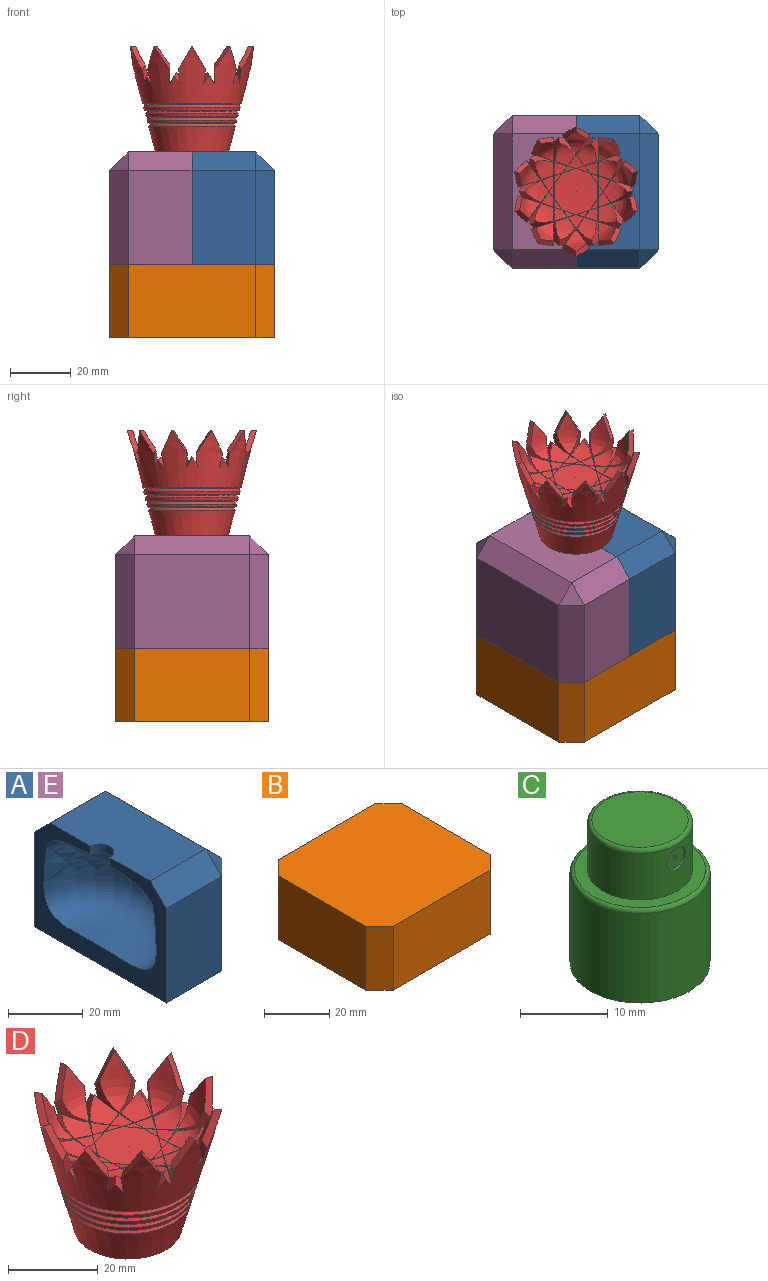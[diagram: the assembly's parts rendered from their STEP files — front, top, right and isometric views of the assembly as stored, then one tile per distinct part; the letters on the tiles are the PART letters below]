
ASSEMBLY  parts=5 mates=5
PART A: 15 faces, bbox 27x50x37 mm
  f0: plane 38x21mm, normal (0,0,1), area 776.5mm2, adj f4,f5,f10,f12,f13
  f1: plane 31x21mm, normal (0,1,0), area 651mm2, adj f3,f5,f9,f12
  f2: plane 31x21mm, normal (0,-1,0), area 651mm2, adj f3,f4,f7,f12
  f3: plane 50x27mm, normal (0,0,-1), area 1314mm2, adj f1,f2,f6,f7,f9,f12
  f4: plane 21x6mm, normal (0,-0.71,0.71), area 178.2mm2, adj f0,f2,f8,f12
  f5: plane 21x6mm, normal (0,0.71,0.71), area 178.2mm2, adj f0,f1,f11,f12
  f6: plane 38x31mm, normal (1,0,0), area 1178mm2, adj f3,f7,f9,f10
  f7: plane 31x6mm, normal (0.71,-0.71,0), area 263mm2, adj f2,f3,f6,f8
  f8: plane 6x6mm, normal (0.58,-0.58,0.58), area 31.2mm2, adj f4,f7,f10
  f9: plane 31x6mm, normal (0.71,0.71,0), area 263mm2, adj f1,f3,f6,f11
  f10: plane 38x6mm, normal (0.71,0,0.71), area 322.4mm2, adj f0,f6,f8,f11
  f11: plane 6x6mm, normal (0.58,0.58,0.58), area 31.2mm2, adj f5,f9,f10
  f12: plane 50x37mm, normal (-1,0,0), area 677.3mm2, adj f0,f1,f2,f3,f4,f5,f13,f14
  f13: cylinder r=3.7mm len=7.4mm, axis (0,0,1), area 30.8mm2, adj f0,f12,f14
  f14: revolved ~42.55x28.46mm, area 2704.3mm2, adj f12,f13
PART B: 10 faces, bbox 54x50x24 mm
  f0: plane 38x24mm, normal (1,0,0), area 912mm2, adj f4,f5,f7,f8
  f1: plane 42x24mm, normal (0,1,0), area 1008mm2, adj f4,f5,f8,f9
  f2: plane 38x24mm, normal (-1,0,0), area 912mm2, adj f4,f5,f6,f9
  f3: plane 42x24mm, normal (0,-1,0), area 1008mm2, adj f4,f5,f6,f7
  f4: plane 54x50mm, normal (0,0,1), area 2628mm2, adj f0,f1,f2,f3,f6,f7,f8,f9
  f5: plane 54x50mm, normal (0,0,-1), area 2628mm2, adj f0,f1,f2,f3,f6,f7,f8,f9
  f6: plane 24x6mm, normal (-0.71,-0.71,0), area 203.6mm2, adj f2,f3,f4,f5
  f7: plane 24x6mm, normal (0.71,-0.71,0), area 203.6mm2, adj f0,f3,f4,f5
  f8: plane 24x6mm, normal (0.71,0.71,0), area 203.6mm2, adj f0,f1,f4,f5
  f9: plane 24x6mm, normal (-0.71,0.71,0), area 203.6mm2, adj f1,f2,f4,f5
PART C: 11 faces, bbox 17.3x17.3x20 mm
  f0: cylinder r=6mm len=12mm, axis (0,0,-1), area 237.9mm2, adj f3,f5,f10
  f1: plane 11x11mm, normal (0,0,1), area 95mm2, adj f10
  f2: cylinder r=8mm len=16mm, axis (0,0,-1), area 628.3mm2, adj f4,f9
  f3: plane 15x15mm, normal (0,0,1), area 63.6mm2, adj f0,f9
  f4: plane 16x16mm, normal (0,0,-1), area 201.1mm2, adj f2
  f5: cylinder r=1.5mm len=3mm, axis (0,-1,0), area 2.9mm2, adj f0,f6
  f6: plane 3x3mm, normal (0,-1,0), area 6.9mm2, adj f5,f8
  f7: plane 0.5x0.5mm, normal (0,-1,0), area 0.2mm2, adj f8
  f8: cylinder r=0.25mm len=4.3mm, axis (0,-1,0), area 6.8mm2, adj f6,f7
  f9: torus R=7.5mm, axis (0,0,1), area 38.6mm2, adj f2,f3
  f10: torus R=5.5mm, axis (0,0,1), area 28.7mm2, adj f0,f1
PART D: 217 faces, bbox 44x44x36.3 mm
  f0: cone r=21.27mm half-angle=14.8deg, axis (0,0,1), area 1549.5mm2, adj f1,f16,f17,f18,f19,f20,f21,f22
  f1: cone r=15.29mm half-angle=67.7deg, axis (0,0,1), area 99mm2, adj f0,f2
  f2: cone r=15.91mm half-angle=38deg, axis (0,0,-1), area 98mm2, adj f1,f3
  f3: cone r=15.65mm half-angle=14.8deg, axis (0,0,1), area 99.1mm2, adj f2,f4
  f4: cone r=14.73mm half-angle=67.7deg, axis (0,0,1), area 95.4mm2, adj f3,f5
  f5: cone r=15.34mm half-angle=38deg, axis (0,0,-1), area 94.5mm2, adj f4,f6
  f6: cone r=15.09mm half-angle=14.8deg, axis (0,0,1), area 95.6mm2, adj f5,f7
  f7: cone r=14.16mm half-angle=67.7deg, axis (0,0,1), area 91.9mm2, adj f6,f8
  f8: cone r=14.78mm half-angle=38deg, axis (0,0,-1), area 90.9mm2, adj f7,f9
  f9: cone r=14.54mm half-angle=14.8deg, axis (0,0,1), area 85mm2, adj f8,f10
  f10: cone r=13.62mm half-angle=67.7deg, axis (0,0,1), area 88.5mm2, adj f9,f11
  f11: cone r=14.23mm half-angle=38deg, axis (0,0,-1), area 87.5mm2, adj f10,f12
  f12: cone r=14.23mm half-angle=14.8deg, axis (0,0,1), area 718.1mm2, adj f11,f13
  f13: plane 24x24mm, normal (0,0,-1), area 225.4mm2, adj f12,f14
  f14: cylinder r=8.5mm len=21mm, axis (0,0,-1), area 1121.5mm2, adj f13,f15
  f15: plane 17x17mm, normal (0,0,-1), area 227mm2, adj f14
  f16: plane 8.04x4.86mm, normal (-0.86,0,0.51), area 14.8mm2, adj f0,f17,f73,f188
  f17: plane 8.04x4.86mm, normal (0.86,0,0.51), area 14.8mm2, adj f0,f16,f70,f188
  f18: plane 8.04x5.58mm, normal (-0.7,0.51,0.51), area 14.8mm2, adj f0,f65,f67,f182
  f19: plane 7.89x7.71mm, normal (0.81,-0.59,0), area 18.8mm2, adj f0,f20,f59,f60,f198
  f20: plane 7.77x4.78mm, normal (-0.7,0.51,0.51), area 15.5mm2, adj f0,f19,f66,f133,f178
  f21: plane 6.38x6.32mm, normal (0.7,0.51,0.51), area 15.5mm2, adj f0,f23,f26,f92,f211
  f22: plane 8.04x4.86mm, normal (0.86,0,0.51), area 14.8mm2, adj f0,f27,f38,f206
  f23: plane 7.89x7.71mm, normal (-0.81,-0.59,0), area 18.8mm2, adj f0,f21,f27,f38,f206
  f24: plane 8.04x5.58mm, normal (-0.7,-0.51,0.51), area 14.8mm2, adj f0,f28,f30,f209
  f25: plane 9.38x7.71mm, normal (1,0,0), area 18.8mm2, adj f0,f26,f28,f30,f209
  f26: plane 8.5x4.17mm, normal (-0.86,0,0.51), area 15.5mm2, adj f0,f21,f25,f110,f211
  f27: plane 8.04x4.86mm, normal (-0.86,0,0.51), area 14.8mm2, adj f0,f22,f23,f206
  f28: plane 8.04x5.52mm, normal (0.7,0.51,0.51), area 14.8mm2, adj f0,f24,f25,f209
  f29: plane 8.47x4.17mm, normal (0.27,0.82,0.51), area 15.5mm2, adj f0,f30,f31,f113,f208
  f30: plane 9x7.71mm, normal (-0.31,-0.95,0), area 18.8mm2, adj f0,f24,f25,f29,f209
  f31: plane 7.77x4.78mm, normal (-0.7,-0.51,0.51), area 15.5mm2, adj f0,f29,f32,f114,f208
  f32: plane 7.89x7.71mm, normal (0.81,0.59,0), area 18.8mm2, adj f0,f31,f34,f35,f207
  f33: plane 7.76x4.44mm, normal (-0.27,0.82,0.51), area 15.5mm2, adj f0,f34,f61,f124,f197
  f34: plane 9x7.71mm, normal (0.31,-0.95,0), area 18.8mm2, adj f0,f32,f33,f36,f207
  f35: plane 8.04x5.12mm, normal (0.27,0.82,0.51), area 14.8mm2, adj f0,f32,f36,f207
  f36: plane 8.04x5.44mm, normal (-0.27,-0.82,0.51), area 14.8mm2, adj f0,f34,f35,f207
  f37: plane 8.04x5.44mm, normal (-0.27,0.82,0.51), area 14.8mm2, adj f0,f59,f60,f198
  f38: plane 7.89x7.71mm, normal (0.81,-0.59,0), area 18.8mm2, adj f0,f22,f23,f39,f206
  f39: plane 6.38x6.32mm, normal (-0.7,0.51,0.51), area 15.5mm2, adj f0,f38,f41,f97,f205
  f40: plane 9.38x7.71mm, normal (-1,0,0), area 18.8mm2, adj f0,f41,f56,f57,f201
  f41: plane 8.5x4.17mm, normal (0.86,0,0.51), area 15.5mm2, adj f0,f39,f40,f99,f205
  f42: plane 8.04x5.58mm, normal (0.7,-0.51,0.51), area 14.8mm2, adj f0,f56,f57,f201
  f43: plane 8.04x5.12mm, normal (-0.27,0.82,0.51), area 14.8mm2, adj f0,f45,f46,f204
  f44: plane 7.77x4.78mm, normal (0.7,-0.51,0.51), area 15.5mm2, adj f0,f46,f58,f120,f200
  f45: plane 8.04x5.44mm, normal (0.27,-0.82,0.51), area 14.8mm2, adj f0,f43,f47,f204
  f46: plane 7.89x7.71mm, normal (-0.81,0.59,0), area 18.8mm2, adj f0,f43,f44,f47,f204
  f47: plane 9x7.71mm, normal (-0.31,-0.95,0), area 18.8mm2, adj f0,f45,f46,f48,f204
  f48: plane 7.76x4.44mm, normal (0.27,0.82,0.51), area 15.5mm2, adj f0,f47,f50,f117,f203
  f49: plane 9x7.71mm, normal (-0.31,0.95,0), area 18.8mm2, adj f0,f50,f54,f55,f202
  f50: plane 7.76x4.44mm, normal (0.27,-0.82,0.51), area 15.5mm2, adj f0,f48,f49,f118,f203
  f51: plane 8.04x5.12mm, normal (-0.27,-0.82,0.51), area 14.8mm2, adj f0,f54,f55,f202
  f52: plane 8.04x5.58mm, normal (0.7,0.51,0.51), area 14.8mm2, adj f0,f62,f63,f191
  f53: plane 7.77x4.78mm, normal (0.7,0.51,0.51), area 15.5mm2, adj f0,f54,f64,f131,f192
  f54: plane 7.89x7.71mm, normal (-0.81,-0.59,0), area 18.8mm2, adj f0,f49,f51,f53,f202
  f55: plane 8.04x5.44mm, normal (0.27,0.82,0.51), area 14.8mm2, adj f0,f49,f51,f202
  f56: plane 9x7.71mm, normal (0.31,-0.95,0), area 18.8mm2, adj f0,f40,f42,f58,f201
  f57: plane 8.04x5.52mm, normal (-0.7,0.51,0.51), area 14.8mm2, adj f0,f40,f42,f201
  f58: plane 8.47x4.17mm, normal (-0.27,0.82,0.51), area 15.5mm2, adj f0,f44,f56,f106,f200
  f59: plane 9x7.71mm, normal (0.31,0.95,0), area 18.8mm2, adj f0,f19,f37,f61,f198
  f60: plane 8.04x5.12mm, normal (0.27,-0.82,0.51), area 14.8mm2, adj f0,f19,f37,f198
  f61: plane 7.76x4.44mm, normal (-0.27,-0.82,0.51), area 15.5mm2, adj f0,f33,f59,f78,f197
  f62: plane 9x7.71mm, normal (0.31,0.95,0), area 18.8mm2, adj f0,f52,f64,f68,f191
  f63: plane 8.04x5.52mm, normal (-0.7,-0.51,0.51), area 14.8mm2, adj f0,f52,f68,f191
  f64: plane 8.47x4.17mm, normal (-0.27,-0.82,0.51), area 15.5mm2, adj f0,f53,f62,f140,f192
  f65: plane 8.04x5.52mm, normal (0.7,-0.51,0.51), area 14.8mm2, adj f0,f18,f75,f182
  f66: plane 8.47x4.17mm, normal (0.27,-0.82,0.51), area 15.5mm2, adj f0,f20,f67,f173,f178
  f67: plane 9x7.71mm, normal (-0.31,0.95,0), area 18.8mm2, adj f0,f18,f66,f75,f182
  f68: plane 9.38x7.71mm, normal (-1,0,0), area 18.8mm2, adj f0,f62,f63,f69,f191
  f69: plane 8.5x4.17mm, normal (0.86,0,0.51), area 15.5mm2, adj f0,f68,f71,f143,f185
  f70: plane 7.89x7.71mm, normal (0.81,0.59,0), area 18.8mm2, adj f0,f17,f71,f73,f188
  f71: plane 6.38x6.32mm, normal (-0.7,-0.51,0.51), area 15.5mm2, adj f0,f69,f70,f168,f185
  f72: plane 6.38x6.32mm, normal (0.7,-0.51,0.51), area 15.5mm2, adj f0,f73,f74,f165,f183
  f73: plane 7.89x7.71mm, normal (-0.81,0.59,0), area 18.8mm2, adj f0,f16,f70,f72,f188
  f74: plane 8.5x4.17mm, normal (-0.86,0,0.51), area 15.5mm2, adj f0,f72,f75,f161,f183
  f75: plane 9.38x7.71mm, normal (1,0,0), area 18.8mm2, adj f0,f65,f67,f74,f182
  f76: plane 2.64x1.99mm, normal (0.81,-0.59,0), area 0.2mm2, adj f77,f125,f127,f195
  f77: plane 2.62x1.98mm, normal (-0.7,0.51,0.51), area 0.3mm2, adj f76,f134,f175,f176
  f78: plane 4.38x3.34mm, normal (0.81,-0.59,0), area 1.4mm2, adj f61,f79,f124,f197
  f79: plane 4.31x3.32mm, normal (-0.7,0.51,0.51), area 1.5mm2, adj f78,f132,f135,f180
  f80: plane 3.03x1.18mm, normal (-0.27,0.82,0.51), area 0.3mm2, adj f81,f87,f88,f216
  f81: plane 3.05x1.18mm, normal (0.31,-0.95,0), area 0.2mm2, adj f80,f82,f96,f214
  f82: plane 3.05x1.18mm, normal (-0.31,-0.95,0), area 0.2mm2, adj f81,f83,f93,f214
  f83: plane 3.03x1.18mm, normal (0.27,0.82,0.51), area 0.3mm2, adj f82,f85,f95,f215
  f84: plane 5.19x2.19mm, normal (-0.27,0.82,0.51), area 0.1mm2, adj f85,f86,f91,f177
  f85: plane 5.19x2.17mm, normal (0.31,-0.95,0), area 0.1mm2, adj f83,f84,f95,f215
  f86: plane 5.19x2.19mm, normal (0.27,0.82,0.51), area 0.1mm2, adj f84,f87,f100,f177
  f87: plane 5.19x2.17mm, normal (-0.31,-0.95,0), area 0.1mm2, adj f80,f86,f88,f216
  f88: plane 2.62x2.01mm, normal (0.7,0.51,0.51), area 0.3mm2, adj f80,f87,f89,f216
  f89: plane 2.64x1.99mm, normal (-0.81,-0.59,0), area 0.2mm2, adj f88,f98,f105,f212
  f90: plane 4.52x3.48mm, normal (0.81,-0.59,0), area 0.1mm2, adj f91,f109,f126,f196
  f91: plane 4.53x3.5mm, normal (-0.7,0.51,0.51), area 0.1mm2, adj f84,f90,f174,f177
  f92: plane 4.38x3.34mm, normal (0.81,-0.59,0), area 1.4mm2, adj f21,f93,f110,f211
  f93: plane 4.33x3.27mm, normal (-0.7,0.51,0.51), area 1.5mm2, adj f82,f92,f96,f214
  f94: plane 2.64x1.99mm, normal (0.81,-0.59,0), area 0.2mm2, adj f95,f108,f111,f210
  f95: plane 2.62x2.01mm, normal (-0.7,0.51,0.51), area 0.3mm2, adj f83,f85,f94,f215
  f96: plane 4.33x3.27mm, normal (0.7,0.51,0.51), area 1.5mm2, adj f81,f93,f97,f214
  f97: plane 4.38x3.34mm, normal (-0.81,-0.59,0), area 1.4mm2, adj f39,f96,f99,f205
  f98: plane 4.97x2.02mm, normal (-0.27,0.82,0.51), area 1.5mm2, adj f89,f99,f107,f212
  f99: plane 5.05x2.03mm, normal (0.31,-0.95,0), area 1.4mm2, adj f41,f97,f98,f205
  f100: plane 4.53x3.5mm, normal (0.7,0.51,0.51), area 0.1mm2, adj f86,f101,f137,f177
  f101: plane 4.52x3.48mm, normal (-0.81,-0.59,0), area 0.1mm2, adj f100,f103,f104,f213
  f102: plane 3.19x0.42mm, normal (-1,0,0), area 0.2mm2, adj f103,f121,f122,f199
  f103: plane 3.18x0.4mm, normal (0.86,0,0.51), area 0.3mm2, adj f101,f102,f104,f213
  f104: plane 3.03x1.23mm, normal (0.27,0.82,0.51), area 0.3mm2, adj f101,f103,f105,f213
  f105: plane 3.05x1.18mm, normal (-0.31,-0.95,0), area 0.2mm2, adj f89,f104,f107,f212
  f106: plane 5.28x1.14mm, normal (-1,0,0), area 1.4mm2, adj f58,f107,f120,f200
  f107: plane 5.2x1.02mm, normal (0.86,0,0.51), area 1.5mm2, adj f98,f105,f106,f212
  f108: plane 3.05x1.18mm, normal (0.31,-0.95,0), area 0.2mm2, adj f94,f109,f112,f210
  f109: plane 3.03x1.23mm, normal (-0.27,0.82,0.51), area 0.3mm2, adj f90,f108,f126,f196
  f110: plane 5.05x2.03mm, normal (-0.31,-0.95,0), area 1.4mm2, adj f26,f92,f111,f211
  f111: plane 4.97x2.02mm, normal (0.27,0.82,0.51), area 1.5mm2, adj f94,f110,f112,f210
  f112: plane 5.2x1.02mm, normal (-0.86,0,0.51), area 1.5mm2, adj f108,f111,f113,f210
  f113: plane 5.28x1.14mm, normal (1,0,0), area 1.4mm2, adj f29,f112,f114,f208
  f114: plane 5.05x2.03mm, normal (0.31,-0.95,0), area 1.4mm2, adj f31,f113,f115,f208
  f115: plane 4.98x2.12mm, normal (-0.27,0.82,0.51), area 1.5mm2, adj f114,f125,f127,f195
  f116: plane 4.31x3.32mm, normal (0.7,-0.51,0.51), area 1.5mm2, adj f117,f121,f122,f199
  f117: plane 4.38x3.34mm, normal (-0.81,0.59,0), area 1.4mm2, adj f48,f116,f118,f203
  f118: plane 4.38x3.34mm, normal (-0.81,-0.59,0), area 1.4mm2, adj f50,f117,f119,f203
  f119: plane 4.31x3.32mm, normal (0.7,0.51,0.51), area 1.5mm2, adj f118,f129,f130,f193
  f120: plane 5.05x2.03mm, normal (-0.31,-0.95,0), area 1.4mm2, adj f44,f106,f121,f200
  f121: plane 4.98x2.12mm, normal (0.27,0.82,0.51), area 1.5mm2, adj f102,f116,f120,f199
  f122: plane 2.64x1.99mm, normal (-0.81,-0.59,0), area 0.2mm2, adj f102,f116,f123,f199
  f123: plane 2.62x1.98mm, normal (0.7,0.51,0.51), area 0.3mm2, adj f122,f128,f136,f194
  f124: plane 4.38x3.34mm, normal (0.81,0.59,0), area 1.4mm2, adj f33,f78,f125,f197
  f125: plane 4.31x3.32mm, normal (-0.7,-0.51,0.51), area 1.5mm2, adj f76,f115,f124,f195
  f126: plane 3.18x0.4mm, normal (-0.86,0,0.51), area 0.3mm2, adj f90,f109,f127,f196
  f127: plane 3.19x0.42mm, normal (1,0,0), area 0.2mm2, adj f76,f115,f126,f195
  f128: plane 2.62x1.98mm, normal (0.7,-0.51,0.51), area 0.3mm2, adj f123,f129,f136,f194
  f129: plane 2.64x1.99mm, normal (-0.81,0.59,0), area 0.2mm2, adj f119,f128,f138,f193
  f130: plane 4.98x2.12mm, normal (0.27,-0.82,0.51), area 1.5mm2, adj f119,f131,f138,f193
  f131: plane 5.05x2.03mm, normal (-0.31,0.95,0), area 1.4mm2, adj f53,f130,f140,f192
  f132: plane 4.98x2.12mm, normal (-0.27,-0.82,0.51), area 1.5mm2, adj f79,f133,f171,f180
  f133: plane 5.05x2.03mm, normal (0.31,0.95,0), area 1.4mm2, adj f20,f132,f173,f178
  f134: plane 2.62x1.98mm, normal (-0.7,-0.51,0.51), area 0.3mm2, adj f77,f135,f175,f176
  f135: plane 2.64x1.99mm, normal (0.81,0.59,0), area 0.2mm2, adj f79,f134,f171,f180
  f136: plane 5.42x0.76mm, normal (-1,0,0), area 0.1mm2, adj f123,f128,f137,f194
  f137: plane 5.42x0.76mm, normal (0.86,0,0.51), area 0.1mm2, adj f100,f136,f147,f177
  f138: plane 3.19x0.42mm, normal (-1,0,0), area 0.2mm2, adj f129,f130,f139,f193
  f139: plane 3.18x0.4mm, normal (0.86,0,0.51), area 0.3mm2, adj f138,f145,f146,f190
  f140: plane 5.28x1.14mm, normal (-1,0,0), area 1.4mm2, adj f64,f131,f141,f192
  f141: plane 5.2x1.02mm, normal (0.86,0,0.51), area 1.5mm2, adj f140,f142,f144,f187
  f142: plane 4.97x2.02mm, normal (-0.27,-0.82,0.51), area 1.5mm2, adj f141,f143,f166,f187
  f143: plane 5.05x2.03mm, normal (0.31,0.95,0), area 1.4mm2, adj f69,f142,f168,f185
  f144: plane 3.05x1.18mm, normal (-0.31,0.95,0), area 0.2mm2, adj f141,f145,f166,f187
  f145: plane 3.03x1.23mm, normal (0.27,-0.82,0.51), area 0.3mm2, adj f139,f144,f146,f190
  f146: plane 4.52x3.48mm, normal (-0.81,0.59,0), area 0.1mm2, adj f139,f145,f147,f190
  f147: plane 4.53x3.5mm, normal (0.7,-0.51,0.51), area 0.1mm2, adj f137,f146,f154,f177
  f148: plane 3.03x1.18mm, normal (0.27,-0.82,0.51), area 0.3mm2, adj f149,f150,f151,f189
  f149: plane 2.62x2.01mm, normal (-0.7,-0.51,0.51), area 0.3mm2, adj f148,f150,f152,f189
  f150: plane 5.19x2.17mm, normal (0.31,0.95,0), area 0.1mm2, adj f148,f149,f157,f189
  f151: plane 3.05x1.18mm, normal (-0.31,0.95,0), area 0.2mm2, adj f148,f153,f164,f184
  f152: plane 2.64x1.99mm, normal (0.81,0.59,0), area 0.2mm2, adj f149,f160,f162,f179
  f153: plane 3.05x1.18mm, normal (0.31,0.95,0), area 0.2mm2, adj f151,f156,f169,f184
  f154: plane 5.19x2.19mm, normal (0.27,-0.82,0.51), area 0.1mm2, adj f147,f155,f157,f177
  f155: plane 5.19x2.17mm, normal (-0.31,0.95,0), area 0.1mm2, adj f154,f156,f167,f186
  f156: plane 3.03x1.18mm, normal (-0.27,-0.82,0.51), area 0.3mm2, adj f153,f155,f167,f186
  f157: plane 5.19x2.19mm, normal (-0.27,-0.82,0.51), area 0.1mm2, adj f150,f154,f159,f177
  f158: plane 4.52x3.48mm, normal (0.81,0.59,0), area 0.1mm2, adj f159,f163,f170,f181
  f159: plane 4.53x3.5mm, normal (-0.7,-0.51,0.51), area 0.1mm2, adj f157,f158,f174,f177
  f160: plane 3.05x1.18mm, normal (0.31,0.95,0), area 0.2mm2, adj f152,f163,f172,f179
  f161: plane 5.05x2.03mm, normal (-0.31,0.95,0), area 1.4mm2, adj f74,f162,f165,f183
  f162: plane 4.97x2.02mm, normal (0.27,-0.82,0.51), area 1.5mm2, adj f152,f161,f172,f179
  f163: plane 3.03x1.23mm, normal (-0.27,-0.82,0.51), area 0.3mm2, adj f158,f160,f170,f181
  f164: plane 4.33x3.27mm, normal (-0.7,-0.51,0.51), area 1.5mm2, adj f151,f165,f169,f184
  f165: plane 4.38x3.34mm, normal (0.81,0.59,0), area 1.4mm2, adj f72,f161,f164,f183
  f166: plane 2.64x1.99mm, normal (-0.81,0.59,0), area 0.2mm2, adj f142,f144,f167,f187
  f167: plane 2.62x2.01mm, normal (0.7,-0.51,0.51), area 0.3mm2, adj f155,f156,f166,f186
  f168: plane 4.38x3.34mm, normal (-0.81,0.59,0), area 1.4mm2, adj f71,f143,f169,f185
  f169: plane 4.33x3.27mm, normal (0.7,-0.51,0.51), area 1.5mm2, adj f153,f164,f168,f184
  f170: plane 3.18x0.4mm, normal (-0.86,0,0.51), area 0.3mm2, adj f158,f163,f171,f181
  f171: plane 3.19x0.42mm, normal (1,0,0), area 0.2mm2, adj f132,f135,f170,f180
  f172: plane 5.2x1.02mm, normal (-0.86,0,0.51), area 1.5mm2, adj f160,f162,f173,f179
  f173: plane 5.28x1.14mm, normal (1,0,0), area 1.4mm2, adj f66,f133,f172,f178
  f174: plane 4.88x0.23mm, normal (-0.86,0,0.51), area 0.1mm2, adj f91,f159,f175,f177
  f175: plane 5.42x0.76mm, normal (1,0,0), area 0.1mm2, adj f77,f134,f174,f176
  f176: revolved ~5.38x1.61mm, area 3.1mm2, adj f77,f134,f175
  f177: revolved ~15.15x15.15mm, area 179.6mm2, adj f84,f86,f91,f100,f137,f147,f154,f157
  f178: revolved ~10.4x10.37mm, area 34.3mm2, adj f20,f66,f133,f173
  f179: revolved ~7.08x6.67mm, area 12.4mm2, adj f152,f160,f162,f172
  f180: revolved ~6.8x5.6mm, area 12.4mm2, adj f79,f132,f135,f171
  f181: revolved ~4.75x3.91mm, area 3.1mm2, adj f158,f163,f170
  f182: revolved ~11.64x9.48mm, area 51.5mm2, adj f18,f65,f67,f75
  f183: revolved ~9.4x9.33mm, area 34.3mm2, adj f72,f74,f161,f165
  f184: revolved ~7.12x4.54mm, area 12.4mm2, adj f151,f153,f164,f169
  f185: revolved ~9.4x9.33mm, area 34.3mm2, adj f69,f71,f143,f168
  f186: revolved ~5.12x2.68mm, area 3.1mm2, adj f155,f156,f167
  f187: revolved ~7.08x6.67mm, area 12.4mm2, adj f141,f142,f144,f166
  f188: revolved ~11.64x7.98mm, area 51.5mm2, adj f16,f17,f70,f73
  f189: revolved ~5.12x2.68mm, area 3.1mm2, adj f148,f149,f150
  f190: revolved ~4.75x3.91mm, area 3.1mm2, adj f139,f145,f146
  f191: revolved ~11.64x9.48mm, area 51.5mm2, adj f52,f62,f63,f68
  f192: revolved ~10.4x10.37mm, area 34.3mm2, adj f53,f64,f131,f140
  f193: revolved ~6.8x5.6mm, area 12.4mm2, adj f119,f129,f130,f138
  f194: revolved ~5.38x1.61mm, area 3.1mm2, adj f123,f128,f136
  f195: revolved ~6.8x5.6mm, area 12.4mm2, adj f76,f115,f125,f127
  f196: revolved ~4.75x3.91mm, area 3.1mm2, adj f90,f109,f126
  f197: revolved ~9.75x8.11mm, area 34.3mm2, adj f33,f61,f78,f124
  f198: revolved ~11.64x8.66mm, area 51.5mm2, adj f19,f37,f59,f60
  f199: revolved ~6.8x5.6mm, area 12.4mm2, adj f102,f116,f121,f122
  f200: revolved ~10.4x10.37mm, area 34.3mm2, adj f44,f58,f106,f120
  f201: revolved ~11.64x9.48mm, area 51.5mm2, adj f40,f42,f56,f57
  f202: revolved ~11.64x8.66mm, area 51.5mm2, adj f49,f51,f54,f55
  f203: revolved ~9.75x8.11mm, area 34.3mm2, adj f48,f50,f117,f118
  f204: revolved ~11.64x8.66mm, area 51.5mm2, adj f43,f45,f46,f47
  f205: revolved ~9.4x9.33mm, area 34.3mm2, adj f39,f41,f97,f99
  f206: revolved ~11.64x7.98mm, area 51.5mm2, adj f22,f23,f27,f38
  f207: revolved ~11.64x8.66mm, area 51.5mm2, adj f32,f34,f35,f36
  f208: revolved ~10.4x10.37mm, area 34.3mm2, adj f29,f31,f113,f114
  f209: revolved ~11.64x9.48mm, area 51.5mm2, adj f24,f25,f28,f30
  f210: revolved ~7.08x6.67mm, area 12.4mm2, adj f94,f108,f111,f112
  f211: revolved ~9.4x9.33mm, area 34.3mm2, adj f21,f26,f92,f110
  f212: revolved ~7.08x6.67mm, area 12.4mm2, adj f89,f98,f105,f107
  f213: revolved ~4.75x3.91mm, area 3.1mm2, adj f101,f103,f104
  f214: revolved ~7.12x4.54mm, area 12.4mm2, adj f81,f82,f93,f96
  f215: revolved ~5.12x2.68mm, area 3.1mm2, adj f83,f85,f95
  f216: revolved ~5.12x2.68mm, area 3.1mm2, adj f80,f87,f88
PART E: same geometry as A
PLACE A t=(-15.48,-6.97,14.95)mm
PLACE B t=(-15.48,-6.97,-9.05)mm fixed
PLACE C t=(-15.48,-6.92,51.95)mm
PLACE D t=(-15.48,-6.92,51.95)mm
PLACE E rot(axis=(0,0,-1),180deg) t=(-15.48,-6.97,14.95)mm
MATE planar E.f3 <-> B.f4  axis (0,0,-1) through (-42.48,-6.97,14.95)mm
MATE planar D.f0 <-> C.f0  axis (0,0,-1) through (-15.48,-6.92,51.95)mm
MATE planar E.f3 <-> B.f4  axis (0,0,-1) through (-42.48,-6.97,14.95)mm
MATE planar A.f13 <-> C.f0  axis (0,0,1) through (-15.48,-6.92,51.95)mm
MATE planar A.f3 <-> B.f4  axis (0,0,-1) through (11.52,-6.97,14.95)mm
